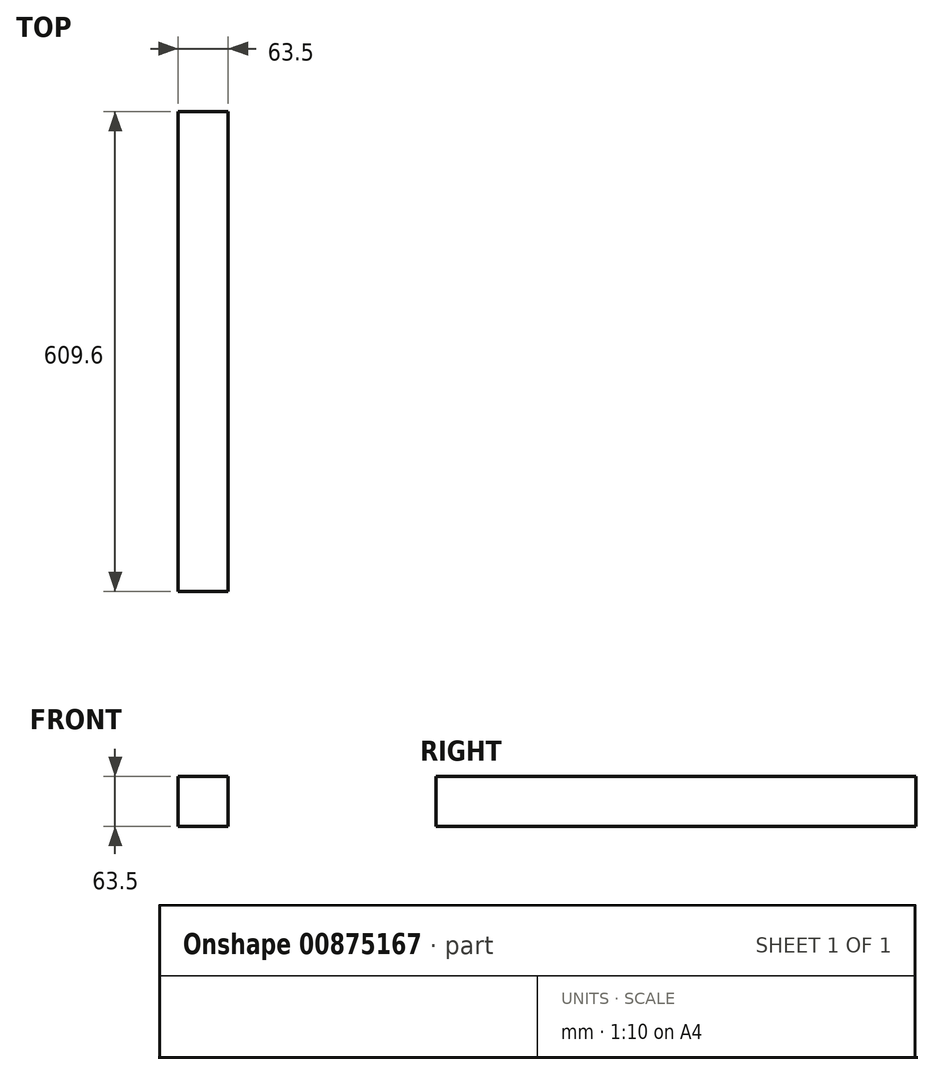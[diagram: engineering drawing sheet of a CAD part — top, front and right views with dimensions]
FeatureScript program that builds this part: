
annotation { "Feature Type Name" : "Feature", "Feature Type Description" : "" }
export const myFeature = defineFeature(function(context is Context, id is Id, definition is map)
    precondition{}
    {
        {
            var Q0;
            Q0=qCreatedBy(makeId("Front.planeOp"),FACE);
            var sketch = newSketch(context, id + "F0", { "sketchPlane" : qUnion([Q0])});
            skLineSegment(sketch, "E0.bottom", {"start": v(-164.57, 68.12) * mm, "end": v(-101.07, 68.12) * mm});
            skLineSegment(sketch, "E0.top", {"start": v(-164.57, 4.62) * mm, "end": v(-101.07, 4.62) * mm});
            skLineSegment(sketch, "E0.left", {"start": v(-164.57, 68.12) * mm, "end": v(-164.57, 4.62) * mm});
            skLineSegment(sketch, "E0.right", {"start": v(-101.07, 68.12) * mm, "end": v(-101.07, 4.62) * mm});
            skSolve(sketch);
        }
        {
            var Q0;
            Q0=makeQuery(id+"F0.imprint","IMPRINT",FACE,{"disambiguationData":[TD([[makeQuery(id+"F0.imprint","IMPRINT",EDGE,{"derivedFrom":sQuery(id+"F0.wireOp",EDGE,"E0.bottom")}),-1.0]])]});
            extrude(context, id + "F1", {"entities" : qUnion([Q0]), "depth" : 1498.6 * mm, "offsetDistance" : 25.4 * mm});
        }
        {
            var Q0;
            Q0=makeQuery(id+"F1.opExtrude","CAP_FACE",FACE,{"disambiguationData":[OSD([sQuery(id+"F0.wireOp",EDGE,"E0.bottom"),sQuery(id+"F0.wireOp",EDGE,"E0.top"),sQuery(id+"F0.wireOp",EDGE,"E0.left"),sQuery(id+"F0.wireOp",EDGE,"E0.right")])],"isStart":true});
            extrude(context, id + "F2", {"entities" : qUnion([Q0]), "operationType" : NewBodyOperationType.REMOVE, "oppositeDirection" : true, "depth" : 1092.2 * mm, "offsetDistance" : 25.4 * mm});
        }
        {
            var Q0;
            Q0=makeQuery(id+"F2.boolean.opBoolean","COPY",FACE,{"derivedFrom":makeQuery(id+"F2.opExtrude","CAP_FACE",FACE,{"disambiguationData":[OSD([sQuery(id+"F0.wireOp",EDGE,"E0.bottom"),sQuery(id+"F0.wireOp",EDGE,"E0.top"),sQuery(id+"F0.wireOp",EDGE,"E0.left"),sQuery(id+"F0.wireOp",EDGE,"E0.right")])],"isStart":false})});
            extrude(context, id + "F3", {"entities" : qUnion([Q0]), "operationType" : NewBodyOperationType.REMOVE, "oppositeDirection" : true, "depth" : 203.2 * mm, "offsetDistance" : 25.4 * mm});
        }
        {
            var Q0;
            Q0=makeQuery(id+"F1.opExtrude","CAP_FACE",FACE,{"disambiguationData":[OSD([sQuery(id+"F0.wireOp",EDGE,"E0.bottom"),sQuery(id+"F0.wireOp",EDGE,"E0.top"),sQuery(id+"F0.wireOp",EDGE,"E0.left"),sQuery(id+"F0.wireOp",EDGE,"E0.right")])],"isStart":false});
            extrude(context, id + "F4", {"entities" : qUnion([Q0]), "operationType" : NewBodyOperationType.REMOVE, "oppositeDirection" : true, "depth" : 177.8 * mm, "offsetDistance" : 25.4 * mm});
        }
        {
            var Q0;
            Q0=makeQuery(id+"F3.boolean.opBoolean","COPY",FACE,{"derivedFrom":makeQuery(id+"F3.opExtrude","CAP_FACE",FACE,{"disambiguationData":[OSD([sQuery(id+"F0.wireOp",EDGE,"E0.bottom"),sQuery(id+"F0.wireOp",EDGE,"E0.top"),sQuery(id+"F0.wireOp",EDGE,"E0.left"),sQuery(id+"F0.wireOp",EDGE,"E0.right")])],"isStart":false})});
            extrude(context, id + "F5", {"entities" : qUnion([Q0]), "operationType" : NewBodyOperationType.ADD, "depth" : 584.2 * mm, "offsetDistance" : 25.4 * mm});
        }
    });
